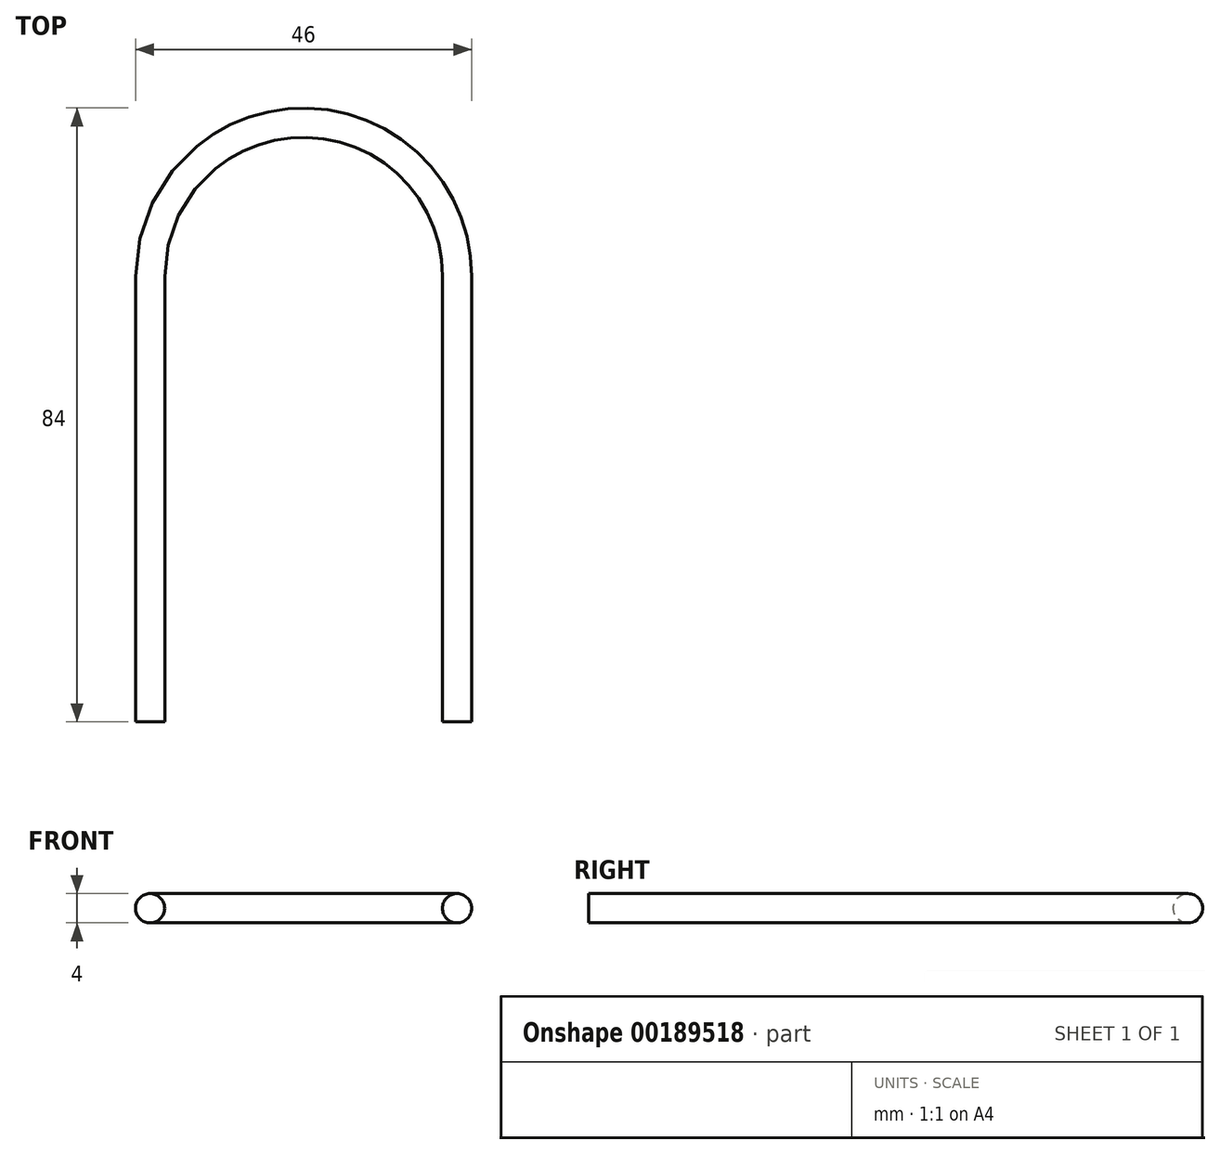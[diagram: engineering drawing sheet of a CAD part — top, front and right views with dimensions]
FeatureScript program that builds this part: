
annotation { "Feature Type Name" : "Feature", "Feature Type Description" : "" }
export const myFeature = defineFeature(function(context is Context, id is Id, definition is map)
    precondition{}
    {
        {
            var Q0;
            Q0=qCreatedBy(makeId("Top.planeOp"),FACE);
            var sketch = newSketch(context, id + "F0", { "sketchPlane" : qUnion([Q0])});
            skLineSegment(sketch, "E0", {"start": v(-21, 0) * mm, "end": v(-21, 61) * mm});
            skArc(sketch, "E1", {"start": v(21, 61) * mm, "mid": v(0, 82) * mm, "end": v(-21, 61) * mm});
            skLineSegment(sketch, "E2", {"start": v(21, 61) * mm, "end": v(21, 0) * mm});
            skSolve(sketch);
        }
        {
            var Q0;
            Q0=qCreatedBy(makeId("Front.planeOp"),FACE);
            var sketch = newSketch(context, id + "F1", { "sketchPlane" : qUnion([Q0])});
            skCircle(sketch, "E3", {"center": v(-21, 0) * mm, "radius": 2 * mm});
            skSolve(sketch);
        }
        {
            var Q0;
            Q0=makeQuery(id+"F1.imprint","IMPRINT",FACE,{"disambiguationData":[TD([[makeQuery(id+"F1.imprint","IMPRINT",EDGE,{"derivedFrom":sQuery(id+"F1.wireOp",EDGE,"E3")}),1.0]])]});
            var Q1;
            Q1=sQuery(id+"F0.wireOp",EDGE,"E0");
            var Q2;
            Q2=sQuery(id+"F0.wireOp",EDGE,"E1");
            var Q3;
            Q3=sQuery(id+"F0.wireOp",EDGE,"E2");
            sweep(context, id + "F2", {"profiles" : qUnion([Q0]), "path" : qUnion([Q1, Q2, Q3])});
        }
    });
